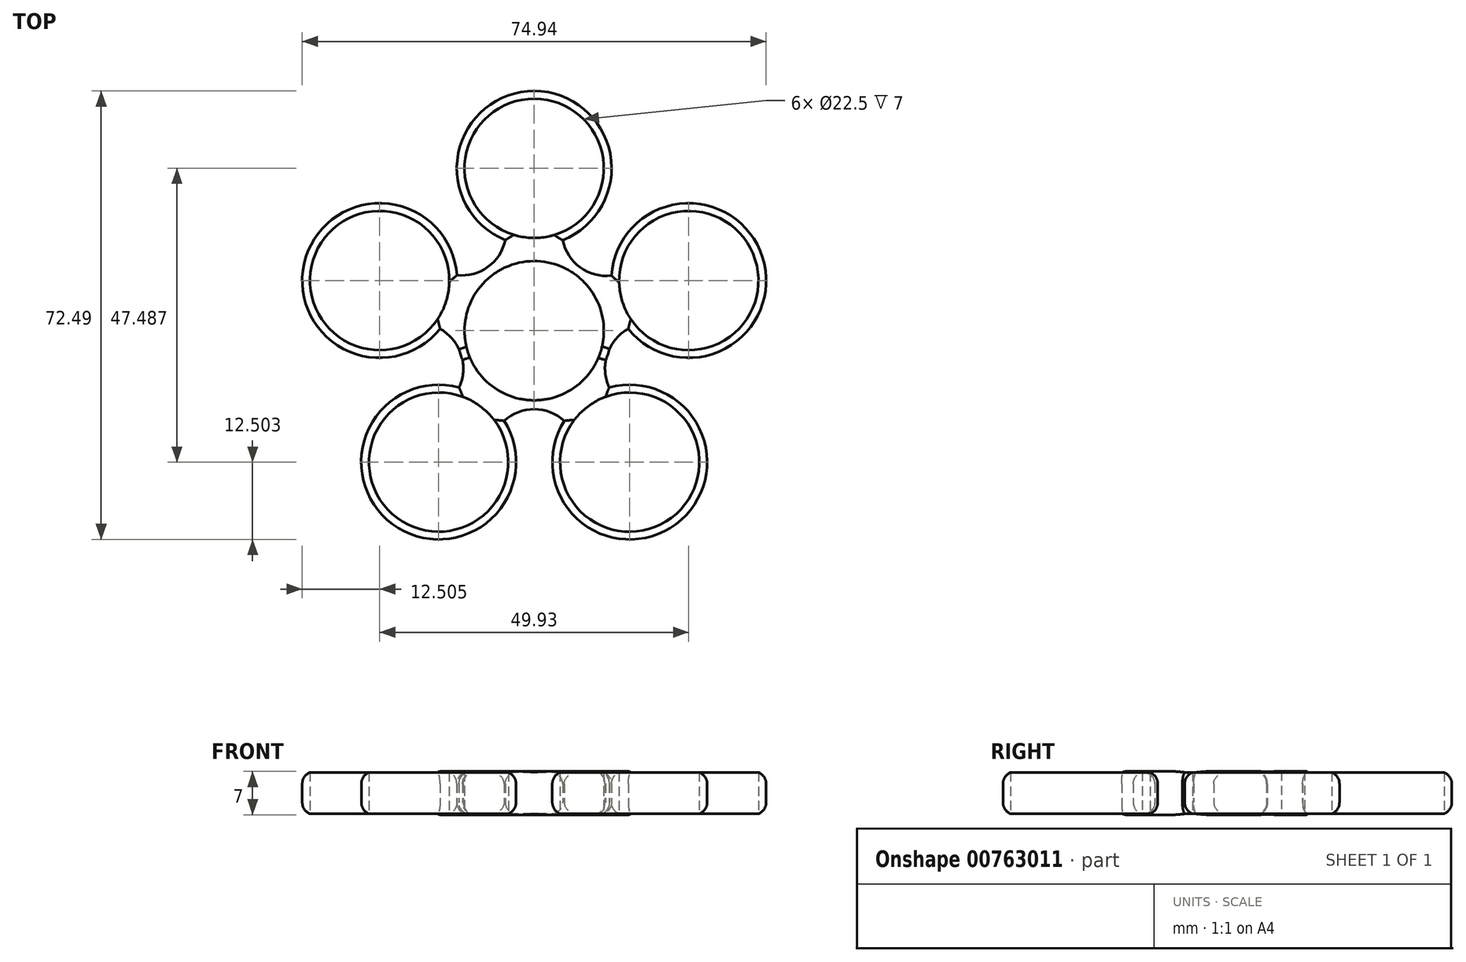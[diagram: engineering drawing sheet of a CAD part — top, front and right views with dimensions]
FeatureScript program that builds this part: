
annotation { "Feature Type Name" : "Feature", "Feature Type Description" : "" }
export const myFeature = defineFeature(function(context is Context, id is Id, definition is map)
    precondition{}
    {
        {
            var Q0;
            Q0=qCreatedBy(makeId("Top.planeOp"),FACE);
            var sketch = newSketch(context, id + "F0", { "sketchPlane" : qUnion([Q0])});
            skCircle(sketch, "E0", {"center": v(0, 0) * mm, "radius": 11.25 * mm});
            skCircle(sketch, "E1", {"center": v(0, 0) * mm, "radius": 12.5 * mm});
            skLineSegment(sketch, "E2", {"start": v(0, 12.5) * mm, "end": v(0, 15) * mm});
            skCircle(sketch, "E3", {"center": v(0, 26.25) * mm, "radius": 11.25 * mm});
            skCircle(sketch, "E4", {"center": v(0, 26.25) * mm, "radius": 12.5 * mm});
            skCircle(sketch, "E5.1.0", {"center": v(-24.97, 8.11) * mm, "radius": 12.5 * mm});
            skCircle(sketch, "E5.1.1", {"center": v(-24.97, 8.11) * mm, "radius": 11.25 * mm});
            skCircle(sketch, "E5.2.0", {"center": v(-15.43, -21.24) * mm, "radius": 12.5 * mm});
            skCircle(sketch, "E5.2.1", {"center": v(-15.43, -21.24) * mm, "radius": 11.25 * mm});
            skCircle(sketch, "E5.3.0", {"center": v(15.43, -21.24) * mm, "radius": 12.5 * mm});
            skCircle(sketch, "E5.3.1", {"center": v(15.43, -21.24) * mm, "radius": 11.25 * mm});
            skCircle(sketch, "E5.4.0", {"center": v(24.97, 8.11) * mm, "radius": 12.5 * mm});
            skCircle(sketch, "E5.4.1", {"center": v(24.97, 8.11) * mm, "radius": 11.25 * mm});
            skArc(sketch, "E6", {"start": v(15.2, 0.3) * mm, "mid": v(11.8, -3.83) * mm, "end": v(12.12, -9.18) * mm});
            skArc(sketch, "E7", {"start": v(-12.5, 8.98) * mm, "mid": v(-7.49, 10.3) * mm, "end": v(-4.68, 14.66) * mm});
            skArc(sketch, "E8.trimOffspring", {"start": v(4.6, 14.63) * mm, "mid": v(7.44, 10.24) * mm, "end": v(12.5, 8.9) * mm});
            skArc(sketch, "E9.trimOffspring", {"start": v(-12.13, -9.18) * mm, "mid": v(-11.8, -3.84) * mm, "end": v(-15.2, 0.3) * mm});
            skArc(sketch, "E10.trimOffspring", {"start": v(4.86, -14.57) * mm, "mid": v(0, -12.68) * mm, "end": v(-4.86, -14.57) * mm});
            skSolve(sketch);
        }
        {
            var Q0;
            Q0 = qSketchRegion(id + "F0", true);
            extrude(context, id + "F1", {"entities" : qUnion([Q0]), "depth" : 7 * mm, "offsetDistance" : 25 * mm});
        }
        {
            var Q0;
            Q0=makeQuery(id+"F1.opExtrude","CAP_EDGE",EDGE,{"disambiguationData":[OSD([sQuery(id+"F0.wireOp",EDGE,"E5.3.0")])],"isStart":false});
            var Q1;
            Q1=makeQuery(id+"F1.opExtrude","CAP_EDGE",EDGE,{"disambiguationData":[OSD([sQuery(id+"F0.wireOp",EDGE,"E10.trimOffspring")])],"isStart":false});
            var Q2;
            Q2=makeQuery(id+"F1.opExtrude","CAP_EDGE",EDGE,{"disambiguationData":[OSD([sQuery(id+"F0.wireOp",EDGE,"E5.2.0")])],"isStart":false});
            var Q3;
            {var subQ0=sQuery(id+"F0.wireOp",EDGE,"E9.trimOffspring");Q3=makeQuery(id+"F1.opExtrude","CAP_EDGE",EDGE,{"disambiguationData":[OSD([subQ0]),TDD([makeQuery(id+"F0.imprint","IMPRINT",EDGE,{"disambiguationData":[TD([[makeQuery(id+"F0.imprint","INTERSECT",VERTEX,{"disambiguationData":[OD(0.0)],"derivedFrom":[sQuery(id+"F0.wireOp",EDGE,"E1"),subQ0]}),1.0]])],"derivedFrom":subQ0})])],"isStart":false});}
            var Q4;
            {var subQ0=sQuery(id+"F0.wireOp",EDGE,"E9.trimOffspring");Q4=makeQuery(id+"F1.opExtrude","CAP_EDGE",EDGE,{"disambiguationData":[OSD([subQ0]),TDD([makeQuery(id+"F0.imprint","IMPRINT",EDGE,{"disambiguationData":[TD([[makeQuery(id+"F0.imprint","INTERSECT",VERTEX,{"derivedFrom":[sQuery(id+"F0.wireOp",EDGE,"E5.1.0"),subQ0]}),1.0]])],"derivedFrom":subQ0})])],"isStart":false});}
            var Q5;
            {var subQ0=sQuery(id+"F0.wireOp",EDGE,"E9.trimOffspring");var subQ1=sQuery(id+"F0.wireOp",EDGE,"E1");Q5=makeQuery(id+"F1.opExtrude","CAP_EDGE",EDGE,{"disambiguationData":[OSD([subQ1]),TDD([makeQuery(id+"F0.imprint","IMPRINT",EDGE,{"disambiguationData":[TD([[makeQuery(id+"F0.imprint","INTERSECT",VERTEX,{"disambiguationData":[OD(0.0)],"derivedFrom":[subQ1,subQ0]}),1.0]])],"derivedFrom":subQ1})])],"isStart":false});}
            var Q6;
            Q6=makeQuery(id+"F1.opExtrude","CAP_EDGE",EDGE,{"disambiguationData":[OSD([sQuery(id+"F0.wireOp",EDGE,"E5.1.0")])],"isStart":false});
            var Q7;
            Q7=makeQuery(id+"F1.opExtrude","CAP_EDGE",EDGE,{"disambiguationData":[OSD([sQuery(id+"F0.wireOp",EDGE,"E7")])],"isStart":false});
            var Q8;
            Q8=makeQuery(id+"F1.opExtrude","CAP_EDGE",EDGE,{"disambiguationData":[OSD([sQuery(id+"F0.wireOp",EDGE,"E4")])],"isStart":false});
            var Q9;
            Q9=makeQuery(id+"F1.opExtrude","CAP_EDGE",EDGE,{"disambiguationData":[OSD([sQuery(id+"F0.wireOp",EDGE,"E8.trimOffspring")])],"isStart":false});
            var Q10;
            Q10=makeQuery(id+"F1.opExtrude","CAP_EDGE",EDGE,{"disambiguationData":[OSD([sQuery(id+"F0.wireOp",EDGE,"E5.4.0")])],"isStart":false});
            var Q11;
            {var subQ0=sQuery(id+"F0.wireOp",EDGE,"E6");Q11=makeQuery(id+"F1.opExtrude","CAP_EDGE",EDGE,{"disambiguationData":[OSD([subQ0]),TDD([makeQuery(id+"F0.imprint","IMPRINT",EDGE,{"disambiguationData":[TD([[makeQuery(id+"F0.imprint","INTERSECT",VERTEX,{"derivedFrom":[sQuery(id+"F0.wireOp",EDGE,"E5.4.0"),subQ0]}),-1.0]])],"derivedFrom":subQ0})])],"isStart":false});}
            var Q12;
            {var subQ0=sQuery(id+"F0.wireOp",EDGE,"E6");Q12=makeQuery(id+"F1.opExtrude","CAP_EDGE",EDGE,{"disambiguationData":[OSD([subQ0]),TDD([makeQuery(id+"F0.imprint","IMPRINT",EDGE,{"disambiguationData":[TD([[makeQuery(id+"F0.imprint","INTERSECT",VERTEX,{"derivedFrom":[sQuery(id+"F0.wireOp",EDGE,"E5.3.0"),subQ0]}),1.0]])],"derivedFrom":subQ0})])],"isStart":false});}
            var Q13;
            {var subQ0=sQuery(id+"F0.wireOp",EDGE,"E6");var subQ1=sQuery(id+"F0.wireOp",EDGE,"E1");Q13=makeQuery(id+"F1.opExtrude","CAP_EDGE",EDGE,{"disambiguationData":[OSD([subQ1]),TDD([makeQuery(id+"F0.imprint","IMPRINT",EDGE,{"disambiguationData":[TD([[makeQuery(id+"F0.imprint","INTERSECT",VERTEX,{"disambiguationData":[OD(0.0)],"derivedFrom":[subQ1,subQ0]}),-1.0]])],"derivedFrom":subQ1})])],"isStart":false});}
            var Q14;
            Q14=makeQuery(id+"F1.opExtrude","CAP_EDGE",EDGE,{"disambiguationData":[OSD([sQuery(id+"F0.wireOp",EDGE,"E4")])],"isStart":true});
            var Q15;
            Q15=makeQuery(id+"F1.opExtrude","CAP_EDGE",EDGE,{"disambiguationData":[OSD([sQuery(id+"F0.wireOp",EDGE,"E7")])],"isStart":true});
            var Q16;
            Q16=makeQuery(id+"F1.opExtrude","CAP_EDGE",EDGE,{"disambiguationData":[OSD([sQuery(id+"F0.wireOp",EDGE,"E5.1.0")])],"isStart":true});
            var Q17;
            Q17=makeQuery(id+"F1.opExtrude","CAP_EDGE",EDGE,{"disambiguationData":[OSD([sQuery(id+"F0.wireOp",EDGE,"E5.2.0")])],"isStart":true});
            var Q18;
            {var subQ0=sQuery(id+"F0.wireOp",EDGE,"E9.trimOffspring");Q18=makeQuery(id+"F1.opExtrude","CAP_EDGE",EDGE,{"disambiguationData":[OSD([subQ0]),TDD([makeQuery(id+"F0.imprint","IMPRINT",EDGE,{"disambiguationData":[TD([[makeQuery(id+"F0.imprint","INTERSECT",VERTEX,{"disambiguationData":[OD(0.0)],"derivedFrom":[sQuery(id+"F0.wireOp",EDGE,"E1"),subQ0]}),1.0]])],"derivedFrom":subQ0})])],"isStart":true});}
            var Q19;
            {var subQ0=sQuery(id+"F0.wireOp",EDGE,"E9.trimOffspring");var subQ1=sQuery(id+"F0.wireOp",EDGE,"E1");Q19=makeQuery(id+"F1.opExtrude","CAP_EDGE",EDGE,{"disambiguationData":[OSD([subQ1]),TDD([makeQuery(id+"F0.imprint","IMPRINT",EDGE,{"disambiguationData":[TD([[makeQuery(id+"F0.imprint","INTERSECT",VERTEX,{"disambiguationData":[OD(0.0)],"derivedFrom":[subQ1,subQ0]}),1.0]])],"derivedFrom":subQ1})])],"isStart":true});}
            var Q20;
            {var subQ0=sQuery(id+"F0.wireOp",EDGE,"E9.trimOffspring");Q20=makeQuery(id+"F1.opExtrude","CAP_EDGE",EDGE,{"disambiguationData":[OSD([subQ0]),TDD([makeQuery(id+"F0.imprint","IMPRINT",EDGE,{"disambiguationData":[TD([[makeQuery(id+"F0.imprint","INTERSECT",VERTEX,{"derivedFrom":[sQuery(id+"F0.wireOp",EDGE,"E5.1.0"),subQ0]}),1.0]])],"derivedFrom":subQ0})])],"isStart":true});}
            var Q21;
            Q21=makeQuery(id+"F1.opExtrude","CAP_EDGE",EDGE,{"disambiguationData":[OSD([sQuery(id+"F0.wireOp",EDGE,"E10.trimOffspring")])],"isStart":true});
            var Q22;
            Q22=makeQuery(id+"F1.opExtrude","CAP_EDGE",EDGE,{"disambiguationData":[OSD([sQuery(id+"F0.wireOp",EDGE,"E5.3.0")])],"isStart":true});
            var Q23;
            {var subQ0=sQuery(id+"F0.wireOp",EDGE,"E6");Q23=makeQuery(id+"F1.opExtrude","CAP_EDGE",EDGE,{"disambiguationData":[OSD([subQ0]),TDD([makeQuery(id+"F0.imprint","IMPRINT",EDGE,{"disambiguationData":[TD([[makeQuery(id+"F0.imprint","INTERSECT",VERTEX,{"derivedFrom":[sQuery(id+"F0.wireOp",EDGE,"E5.4.0"),subQ0]}),-1.0]])],"derivedFrom":subQ0})])],"isStart":true});}
            var Q24;
            {var subQ0=sQuery(id+"F0.wireOp",EDGE,"E6");var subQ1=sQuery(id+"F0.wireOp",EDGE,"E1");Q24=makeQuery(id+"F1.opExtrude","CAP_EDGE",EDGE,{"disambiguationData":[OSD([subQ1]),TDD([makeQuery(id+"F0.imprint","IMPRINT",EDGE,{"disambiguationData":[TD([[makeQuery(id+"F0.imprint","INTERSECT",VERTEX,{"disambiguationData":[OD(0.0)],"derivedFrom":[subQ1,subQ0]}),-1.0]])],"derivedFrom":subQ1})])],"isStart":true});}
            var Q25;
            {var subQ0=sQuery(id+"F0.wireOp",EDGE,"E6");Q25=makeQuery(id+"F1.opExtrude","CAP_EDGE",EDGE,{"disambiguationData":[OSD([subQ0]),TDD([makeQuery(id+"F0.imprint","IMPRINT",EDGE,{"disambiguationData":[TD([[makeQuery(id+"F0.imprint","INTERSECT",VERTEX,{"derivedFrom":[sQuery(id+"F0.wireOp",EDGE,"E5.3.0"),subQ0]}),1.0]])],"derivedFrom":subQ0})])],"isStart":true});}
            var Q26;
            Q26=makeQuery(id+"F1.opExtrude","CAP_EDGE",EDGE,{"disambiguationData":[OSD([sQuery(id+"F0.wireOp",EDGE,"E8.trimOffspring")])],"isStart":true});
            var Q27;
            Q27=makeQuery(id+"F1.opExtrude","CAP_EDGE",EDGE,{"disambiguationData":[OSD([sQuery(id+"F0.wireOp",EDGE,"E5.4.0")])],"isStart":true});
            fillet(context, id + "F2", {"entities" : qUnion([Q0, Q1, Q2, Q3, Q4, Q5, Q6, Q7, Q8, Q9, Q10, Q11, Q12, Q13, Q14, Q15, Q16, Q17, Q18, Q19, Q20, Q21, Q22, Q23, Q24, Q25, Q26, Q27]), "tangentPropagation" : true, "radius" : 2 * mm, "defaultsChanged" : false, "vertexSettings" : [], "allowEdgeOverflow" : false});
        }
    });
